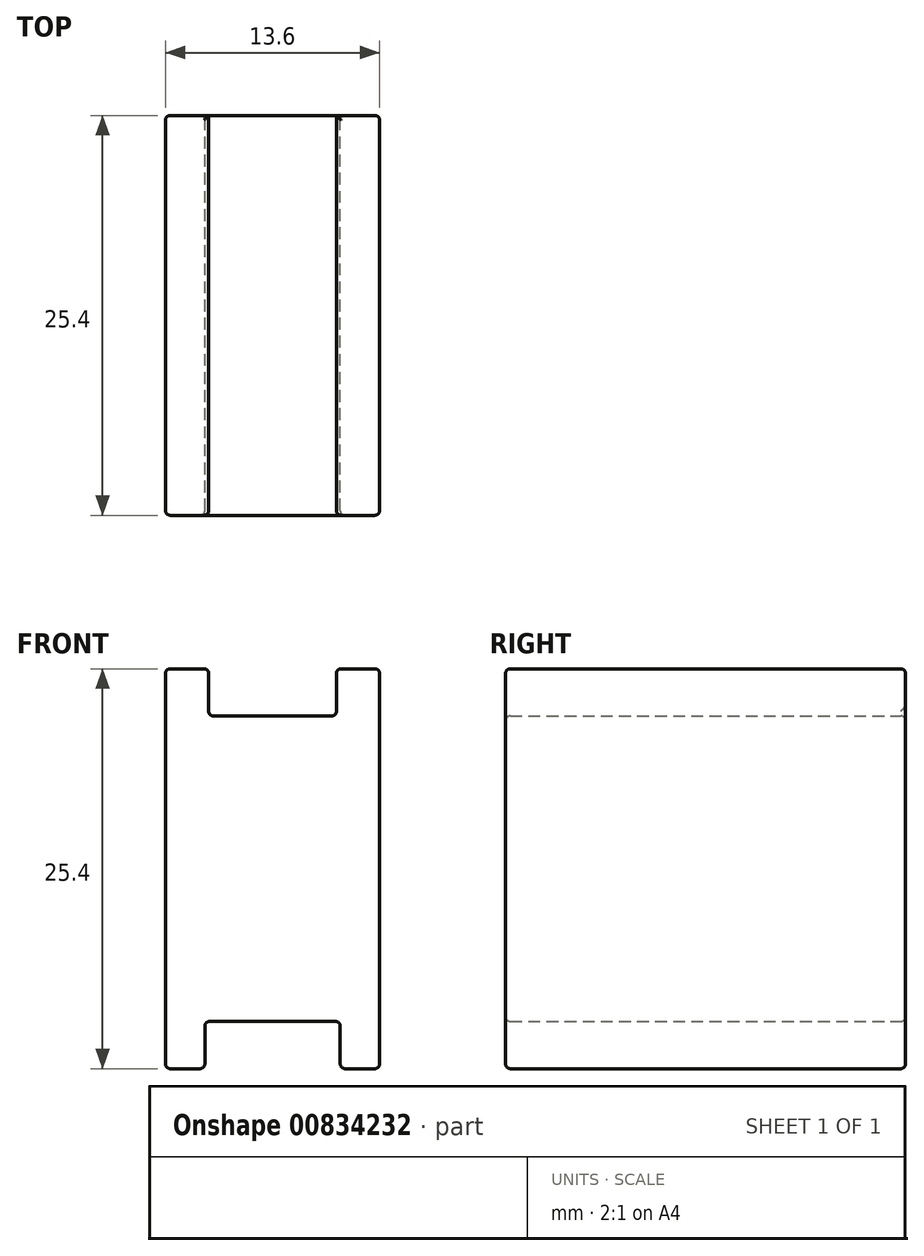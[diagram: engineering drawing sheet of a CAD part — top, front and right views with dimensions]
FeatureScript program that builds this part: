
annotation { "Feature Type Name" : "Feature", "Feature Type Description" : "" }
export const myFeature = defineFeature(function(context is Context, id is Id, definition is map)
    precondition{}
    {
        {
            var Q0;
            Q0=qCreatedBy(makeId("Front.planeOp"),FACE);
            var sketch = newSketch(context, id + "F0", { "sketchPlane" : qUnion([Q0])});
            skLineSegment(sketch, "E0", {"start": v(0, 0) * mm, "end": v(2.5, 0) * mm});
            skLineSegment(sketch, "E1", {"start": v(13.6, 0) * mm, "end": v(13.6, 25.4) * mm});
            skLineSegment(sketch, "E2", {"start": v(0, 25.4) * mm, "end": v(0, 0) * mm});
            skLineSegment(sketch, "E3", {"start": v(13.6, 25.4) * mm, "end": v(10.86, 25.4) * mm});
            skLineSegment(sketch, "E4", {"start": v(2.75, 25.4) * mm, "end": v(2.75, 22.4) * mm});
            skLineSegment(sketch, "E5", {"start": v(10.86, 22.4) * mm, "end": v(2.75, 22.4) * mm});
            skLineSegment(sketch, "E6", {"start": v(10.86, 22.4) * mm, "end": v(10.86, 25.4) * mm});
            skLineSegment(sketch, "E7", {"start": v(2.75, 25.4) * mm, "end": v(0, 25.4) * mm});
            skLineSegment(sketch, "E8", {"start": v(11.1, 0) * mm, "end": v(11.1, 3) * mm});
            skLineSegment(sketch, "E9", {"start": v(11.1, 3) * mm, "end": v(2.5, 3) * mm});
            skLineSegment(sketch, "E10", {"start": v(2.5, 3) * mm, "end": v(2.5, 0) * mm});
            skLineSegment(sketch, "E11.trimOffspring", {"start": v(11.1, 0) * mm, "end": v(13.6, 0) * mm});
            skSolve(sketch);
        }
        {
            var Q0;
            Q0=makeQuery(id+"F0.imprint","IMPRINT",FACE,{"disambiguationData":[TD([[makeQuery(id+"F0.imprint","IMPRINT",EDGE,{"derivedFrom":sQuery(id+"F0.wireOp",EDGE,"E0")}),1.0]])]});
            extrude(context, id + "F1", {"entities" : qUnion([Q0]), "endBound" : BoundingType.SYMMETRIC, "depth" : 25.4 * mm, "offsetDistance" : 25.4 * mm});
        }
        {
            var Q0;
            Q0=makeQuery(id+"F1.opExtrude","CAP_EDGE",EDGE,{"disambiguationData":[OSD([sQuery(id+"F0.wireOp",EDGE,"ilO5W2yG-baNr-48Z5-DJhf-DssQeV1veOfj")])],"isStart":true});
            var Q1;
            Q1=makeQuery(id+"F1.opExtrude","SWEPT_EDGE",EDGE,{"disambiguationData":[OSD([sQuery(id+"F0.wireOp",EDGE,"ilO5W2yG-baNr-48Z5-DJhf-DssQeV1veOfj"),sQuery(id+"F0.wireOp",EDGE,"E2")])]});
            var Q2;
            Q2=makeQuery(id+"F1.opExtrude","CAP_EDGE",EDGE,{"disambiguationData":[OSD([sQuery(id+"F0.wireOp",EDGE,"E2")])],"isStart":true});
            var Q3;
            Q3=makeQuery(id+"F1.opExtrude","CAP_EDGE",EDGE,{"disambiguationData":[OSD([sQuery(id+"F0.wireOp",EDGE,"E2")])],"isStart":false});
            var Q4;
            Q4=makeQuery(id+"F1.opExtrude","SWEPT_EDGE",EDGE,{"disambiguationData":[OSD([sQuery(id+"F0.wireOp",EDGE,"E0"),sQuery(id+"F0.wireOp",EDGE,"E2")])]});
            var Q5;
            Q5=makeQuery(id+"F1.opExtrude","CAP_EDGE",EDGE,{"disambiguationData":[OSD([sQuery(id+"F0.wireOp",EDGE,"E0")])],"isStart":false});
            var Q6;
            Q6=makeQuery(id+"F1.opExtrude","CAP_EDGE",EDGE,{"disambiguationData":[OSD([sQuery(id+"F0.wireOp",EDGE,"ilO5W2yG-baNr-48Z5-DJhf-DssQeV1veOfj")])],"isStart":false});
            var Q7;
            Q7=makeQuery(id+"F1.opExtrude","SWEPT_EDGE",EDGE,{"disambiguationData":[OSD([sQuery(id+"F0.wireOp",EDGE,"zzgsU6cx-reQK-HZsK-n6Hj-6ksNgIGA4Zcc"),sQuery(id+"F0.wireOp",EDGE,"ilO5W2yG-baNr-48Z5-DJhf-DssQeV1veOfj")])]});
            var Q8;
            Q8=makeQuery(id+"F1.opExtrude","CAP_EDGE",EDGE,{"disambiguationData":[OSD([sQuery(id+"F0.wireOp",EDGE,"zzgsU6cx-reQK-HZsK-n6Hj-6ksNgIGA4Zcc")])],"isStart":true});
            var Q9;
            Q9=makeQuery(id+"F1.opExtrude","CAP_EDGE",EDGE,{"disambiguationData":[OSD([sQuery(id+"F0.wireOp",EDGE,"zzgsU6cx-reQK-HZsK-n6Hj-6ksNgIGA4Zcc")])],"isStart":false});
            var Q10;
            Q10=makeQuery(id+"F1.opExtrude","SWEPT_EDGE",EDGE,{"disambiguationData":[OSD([sQuery(id+"F0.wireOp",EDGE,"UBfP8Ycf-qK2W-9caz-WPxZ-FHVW1bi65l4C"),sQuery(id+"F0.wireOp",EDGE,"zzgsU6cx-reQK-HZsK-n6Hj-6ksNgIGA4Zcc")])]});
            var Q11;
            Q11=makeQuery(id+"F1.opExtrude","CAP_EDGE",EDGE,{"disambiguationData":[OSD([sQuery(id+"F0.wireOp",EDGE,"UBfP8Ycf-qK2W-9caz-WPxZ-FHVW1bi65l4C")])],"isStart":false});
            var Q12;
            Q12=makeQuery(id+"F1.opExtrude","CAP_EDGE",EDGE,{"disambiguationData":[OSD([sQuery(id+"F0.wireOp",EDGE,"UBfP8Ycf-qK2W-9caz-WPxZ-FHVW1bi65l4C")])],"isStart":true});
            var Q13;
            Q13=makeQuery(id+"F1.opExtrude","SWEPT_EDGE",EDGE,{"disambiguationData":[OSD([sQuery(id+"F0.wireOp",EDGE,"E1"),sQuery(id+"F0.wireOp",EDGE,"UBfP8Ycf-qK2W-9caz-WPxZ-FHVW1bi65l4C")])]});
            var Q14;
            Q14=makeQuery(id+"F1.opExtrude","CAP_EDGE",EDGE,{"disambiguationData":[OSD([sQuery(id+"F0.wireOp",EDGE,"E1")])],"isStart":false});
            var Q15;
            Q15=makeQuery(id+"F1.opExtrude","CAP_EDGE",EDGE,{"disambiguationData":[OSD([sQuery(id+"F0.wireOp",EDGE,"E1")])],"isStart":true});
            var Q16;
            Q16=makeQuery(id+"F1.opExtrude","SWEPT_EDGE",EDGE,{"disambiguationData":[OSD([sQuery(id+"F0.wireOp",EDGE,"E0"),sQuery(id+"F0.wireOp",EDGE,"E1")])]});
            var Q17;
            Q17=makeQuery(id+"F1.opExtrude","CAP_EDGE",EDGE,{"disambiguationData":[OSD([sQuery(id+"F0.wireOp",EDGE,"E0")])],"isStart":true});
            var Q18;
            Q18=makeQuery(id+"F1.opExtrude","CAP_EDGE",EDGE,{"disambiguationData":[OSD([sQuery(id+"F0.wireOp",EDGE,"E5")])],"isStart":false});
            var Q19;
            Q19=makeQuery(id+"F1.opExtrude","CAP_EDGE",EDGE,{"disambiguationData":[OSD([sQuery(id+"F0.wireOp",EDGE,"E4")])],"isStart":false});
            var Q20;
            Q20=makeQuery(id+"F1.opExtrude","SWEPT_EDGE",EDGE,{"disambiguationData":[OSD([sQuery(id+"F0.wireOp",EDGE,"E4"),sQuery(id+"F0.wireOp",EDGE,"E7")])]});
            var Q21;
            Q21=makeQuery(id+"F1.opExtrude","CAP_EDGE",EDGE,{"disambiguationData":[OSD([sQuery(id+"F0.wireOp",EDGE,"E6")])],"isStart":false});
            var Q22;
            Q22=makeQuery(id+"F1.opExtrude","SWEPT_EDGE",EDGE,{"disambiguationData":[OSD([sQuery(id+"F0.wireOp",EDGE,"E3"),sQuery(id+"F0.wireOp",EDGE,"E6")])]});
            var Q23;
            Q23=makeQuery(id+"F1.opExtrude","SWEPT_EDGE",EDGE,{"disambiguationData":[OSD([sQuery(id+"F0.wireOp",EDGE,"E4"),sQuery(id+"F0.wireOp",EDGE,"E5")])]});
            var Q24;
            Q24=makeQuery(id+"F1.opExtrude","CAP_EDGE",EDGE,{"disambiguationData":[OSD([sQuery(id+"F0.wireOp",EDGE,"E5")])],"isStart":true});
            var Q25;
            Q25=makeQuery(id+"F1.opExtrude","SWEPT_EDGE",EDGE,{"disambiguationData":[OSD([sQuery(id+"F0.wireOp",EDGE,"E5"),sQuery(id+"F0.wireOp",EDGE,"E6")])]});
            var Q26;
            Q26=makeQuery(id+"F1.opExtrude","SWEPT_EDGE",EDGE,{"disambiguationData":[OSD([sQuery(id+"F0.wireOp",EDGE,"E9"),sQuery(id+"F0.wireOp",EDGE,"E10")])]});
            var Q27;
            Q27=makeQuery(id+"F1.opExtrude","CAP_EDGE",EDGE,{"disambiguationData":[OSD([sQuery(id+"F0.wireOp",EDGE,"E10")])],"isStart":false});
            var Q28;
            Q28=makeQuery(id+"F1.opExtrude","CAP_EDGE",EDGE,{"disambiguationData":[OSD([sQuery(id+"F0.wireOp",EDGE,"E9")])],"isStart":false});
            var Q29;
            Q29=makeQuery(id+"F1.opExtrude","CAP_EDGE",EDGE,{"disambiguationData":[OSD([sQuery(id+"F0.wireOp",EDGE,"E8")])],"isStart":false});
            var Q30;
            Q30=makeQuery(id+"F1.opExtrude","SWEPT_EDGE",EDGE,{"disambiguationData":[OSD([sQuery(id+"F0.wireOp",EDGE,"E8"),sQuery(id+"F0.wireOp",EDGE,"E11.trimOffspring")])]});
            var Q31;
            Q31=makeQuery(id+"F1.opExtrude","CAP_EDGE",EDGE,{"disambiguationData":[OSD([sQuery(id+"F0.wireOp",EDGE,"E11.trimOffspring")])],"isStart":false});
            var Q32;
            Q32=makeQuery(id+"F1.opExtrude","CAP_EDGE",EDGE,{"disambiguationData":[OSD([sQuery(id+"F0.wireOp",EDGE,"E10")])],"isStart":true});
            var Q33;
            Q33=makeQuery(id+"F1.opExtrude","CAP_EDGE",EDGE,{"disambiguationData":[OSD([sQuery(id+"F0.wireOp",EDGE,"E9")])],"isStart":true});
            var Q34;
            Q34=makeQuery(id+"F1.opExtrude","CAP_EDGE",EDGE,{"disambiguationData":[OSD([sQuery(id+"F0.wireOp",EDGE,"E8")])],"isStart":true});
            var Q35;
            Q35=makeQuery(id+"F1.opExtrude","SWEPT_EDGE",EDGE,{"disambiguationData":[OSD([sQuery(id+"F0.wireOp",EDGE,"E8"),sQuery(id+"F0.wireOp",EDGE,"E9")])]});
            var Q36;
            Q36=makeQuery(id+"F1.opExtrude","CAP_EDGE",EDGE,{"disambiguationData":[OSD([sQuery(id+"F0.wireOp",EDGE,"E3")])],"isStart":false});
            var Q37;
            Q37=makeQuery(id+"F1.opExtrude","CAP_EDGE",EDGE,{"disambiguationData":[OSD([sQuery(id+"F0.wireOp",EDGE,"E7")])],"isStart":false});
            var Q38;
            Q38=makeQuery(id+"F1.opExtrude","CAP_EDGE",EDGE,{"disambiguationData":[OSD([sQuery(id+"F0.wireOp",EDGE,"E7")])],"isStart":true});
            var Q39;
            Q39=makeQuery(id+"F1.opExtrude","CAP_EDGE",EDGE,{"disambiguationData":[OSD([sQuery(id+"F0.wireOp",EDGE,"E3")])],"isStart":true});
            var Q40;
            Q40=makeQuery(id+"F1.opExtrude","CAP_EDGE",EDGE,{"disambiguationData":[OSD([sQuery(id+"F0.wireOp",EDGE,"E11.trimOffspring")])],"isStart":true});
            fillet(context, id + "F2", {"entities" : qUnion([Q0, Q1, Q2, Q3, Q4, Q5, Q6, Q7, Q8, Q9, Q10, Q11, Q12, Q13, Q14, Q15, Q16, Q17, Q18, Q19, Q20, Q21, Q22, Q23, Q24, Q25, Q26, Q27, Q28, Q29, Q30, Q31, Q32, Q33, Q34, Q35, Q36, Q37, Q38, Q39, Q40]), "radius" : .3 * mm, "tangentPropagation" : true, "allowEdgeOverflow" : false});
        }
    });
